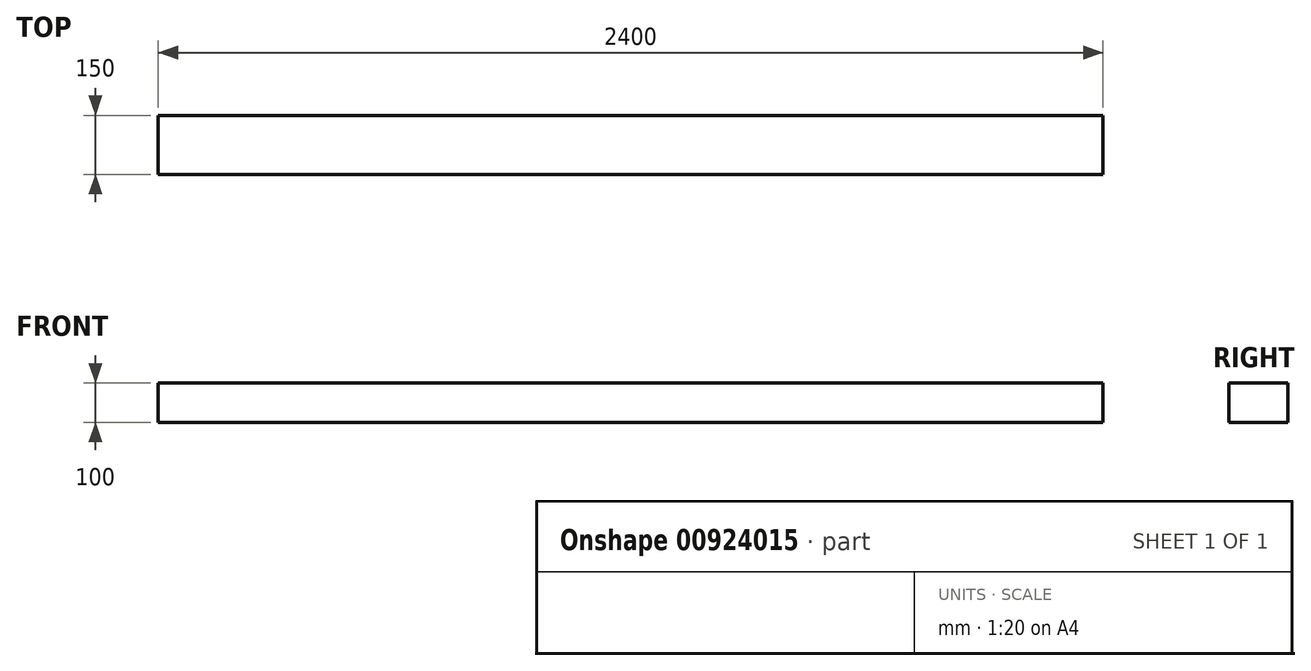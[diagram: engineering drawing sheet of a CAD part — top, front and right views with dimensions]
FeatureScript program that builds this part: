
annotation { "Feature Type Name" : "Feature", "Feature Type Description" : "" }
export const myFeature = defineFeature(function(context is Context, id is Id, definition is map)
    precondition{}
    {
        {
            var Q0;
            Q0=qCreatedBy(makeId("Right.planeOp"),FACE);
            var sketch = newSketch(context, id + "F0", { "sketchPlane" : qUnion([Q0])});
            skLineSegment(sketch, "E0.bottom", {"start": v(0, 0) * mm, "end": v(150, 0) * mm});
            skLineSegment(sketch, "E0.top", {"start": v(0, 100) * mm, "end": v(150, 100) * mm});
            skLineSegment(sketch, "E0.left", {"start": v(0, 0) * mm, "end": v(0, 100) * mm});
            skLineSegment(sketch, "E0.right", {"start": v(150, 0) * mm, "end": v(150, 100) * mm});
            skSolve(sketch);
        }
        {
            var Q0;
            Q0=qSketchRegion(id+"F0",true);
            extrude(context, id + "F1", {"entities" : qUnion([Q0]), "depth" : 2400 * mm, "offsetDistance" : 25 * mm});
        }
    });
